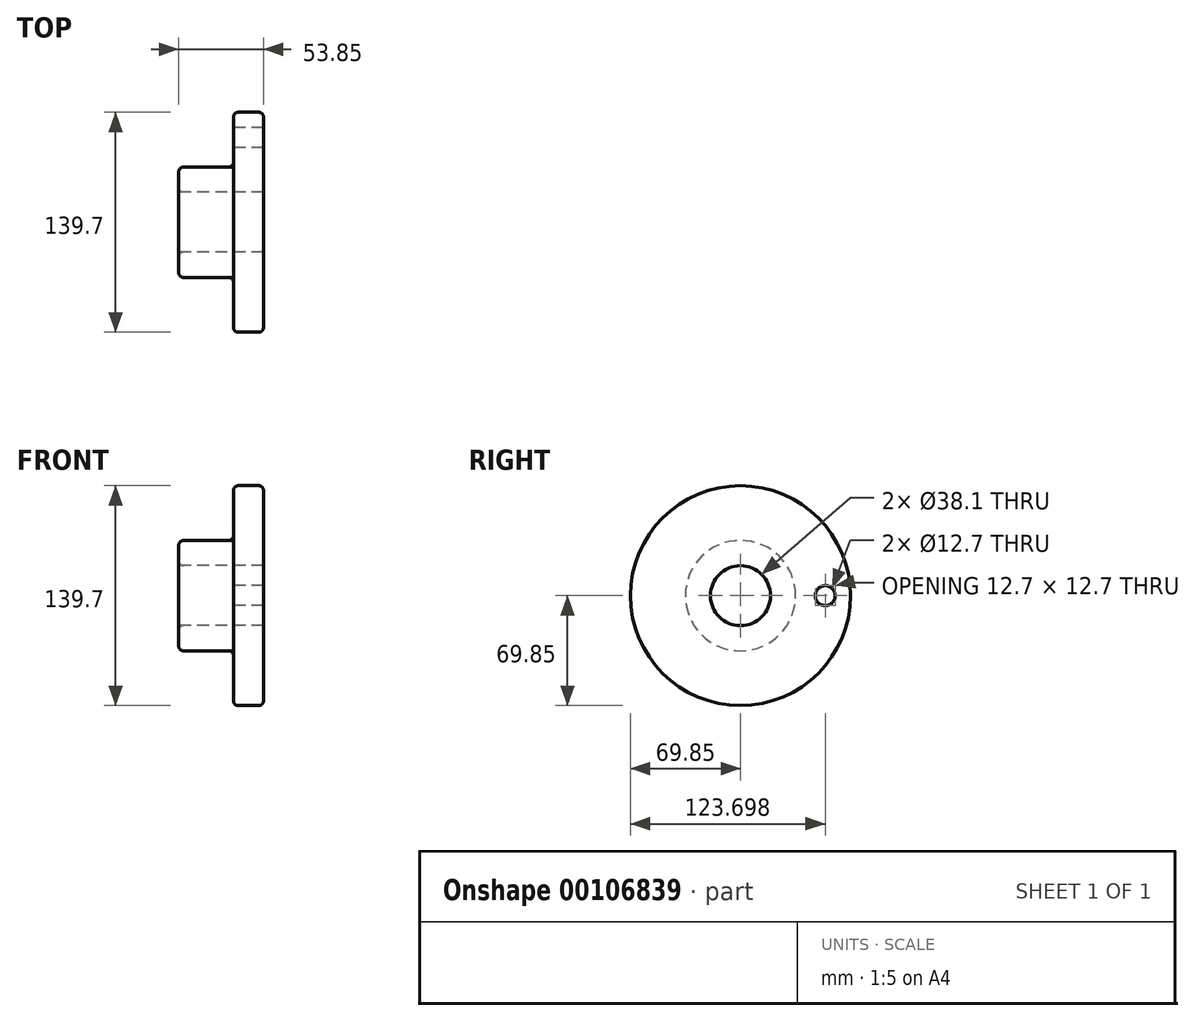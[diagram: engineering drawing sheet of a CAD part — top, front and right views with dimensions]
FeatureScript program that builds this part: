
annotation { "Feature Type Name" : "Feature", "Feature Type Description" : "" }
export const myFeature = defineFeature(function(context is Context, id is Id, definition is map)
    precondition{}
    {
        {
            var Q0;
            Q0=qCreatedBy(makeId("Front.planeOp"),FACE);
            var sketch = newSketch(context, id + "F0", { "sketchPlane" : qUnion([Q0])});
            skLineSegment(sketch, "E0", {"start": v(0, 0) * mm, "end": v(76.2, 0) * mm, "construction": true});
            skLineSegment(sketch, "E1", {"start": v(53.85, 69.85) * mm, "end": v(53.85, 19.05) * mm});
            skLineSegment(sketch, "E2", {"start": v(53.85, 19.05) * mm, "end": v(0, 19.05) * mm});
            skLineSegment(sketch, "E3", {"start": v(0, 19.05) * mm, "end": v(0, 35.05) * mm});
            skLineSegment(sketch, "E4", {"start": v(0, 35.05) * mm, "end": v(34.8, 35.05) * mm});
            skLineSegment(sketch, "E5", {"start": v(34.8, 35.05) * mm, "end": v(34.8, 69.85) * mm});
            skLineSegment(sketch, "E6", {"start": v(34.8, 69.85) * mm, "end": v(53.85, 69.85) * mm});
            skSolve(sketch);
        }
        {
            var Q0;
            Q0 = qSketchRegion(id + "F0", true);
            var Q1;
            Q1=sQuery(id+"F0.wireOp",EDGE,"E0");
            revolve(context, id + "F1", {"entities" : qUnion([Q0]), "axis" : qUnion([Q1]), "revolveType" : RevolveType.FULL});
        }
        {
            var Q0;
            Q0 = qSketchRegion(id + "F0", true);
            var Q1;
            Q1=sQuery(id+"F0.wireOp",EDGE,"E0");
            revolve(context, id + "F2", {"entities" : qUnion([Q0]), "axis" : qUnion([Q1]), "revolveType" : RevolveType.FULL});
        }
        {
            var Q0;
            Q0=makeQuery(id+"F1.opRevolve","SWEPT_FACE",FACE,{"disambiguationData":[OSD([sQuery(id+"F0.wireOp",EDGE,"E5")])]});
            var sketch = newSketch(context, id + "F3", { "sketchPlane" : qUnion([Q0])});
            skCircle(sketch, "E7", {"center": v(0, 0) * mm, "radius": 53.85 * mm, "construction": true});
            skCircle(sketch, "E8", {"center": v(-53.85, 0) * mm, "radius": 6.35 * mm});
            skSolve(sketch);
        }
        {
            var Q0;
            Q0 = qSketchRegion(id + "F3", true);
            extrude(context, id + "F4", {"entities" : qUnion([Q0]), "operationType" : NewBodyOperationType.REMOVE, "endBound" : BoundingType.THROUGH_ALL, "oppositeDirection" : true, "depth" : 25.4 * mm});
        }
        {
            var Q0;
            Q0=makeQuery(id+"F1.opRevolve","SWEPT_FACE",FACE,{"disambiguationData":[OSD([sQuery(id+"F0.wireOp",EDGE,"E6")])]});
            var Q1;
            Q1=makeQuery(id+"F2.opRevolve","SWEPT_FACE",FACE,{"disambiguationData":[OSD([sQuery(id+"F0.wireOp",EDGE,"E6")])]});
            fillet(context, id + "F5", {"entities" : qUnion([Q0, Q1]), "radius" : 3.05 * mm, "tangentPropagation" : true, "allowEdgeOverflow" : false});
        }
        {
            var Q0;
            Q0=makeQuery(id+"F2.opRevolve","SWEPT_FACE",FACE,{"disambiguationData":[OSD([sQuery(id+"F0.wireOp",EDGE,"E3")])]});
            fillet(context, id + "F6", {"entities" : qUnion([Q0]), "radius" : 3.05 * mm, "allowEdgeOverflow" : false});
        }
        {
            var Q0;
            Q0=makeQuery(id+"F1.opRevolve","SWEPT_FACE",FACE,{"disambiguationData":[OSD([sQuery(id+"F0.wireOp",EDGE,"E4")])]});
            fillet(context, id + "F7", {"entities" : qUnion([Q0]), "radius" : 3.05 * mm, "tangentPropagation" : true, "allowEdgeOverflow" : false});
        }
    });
